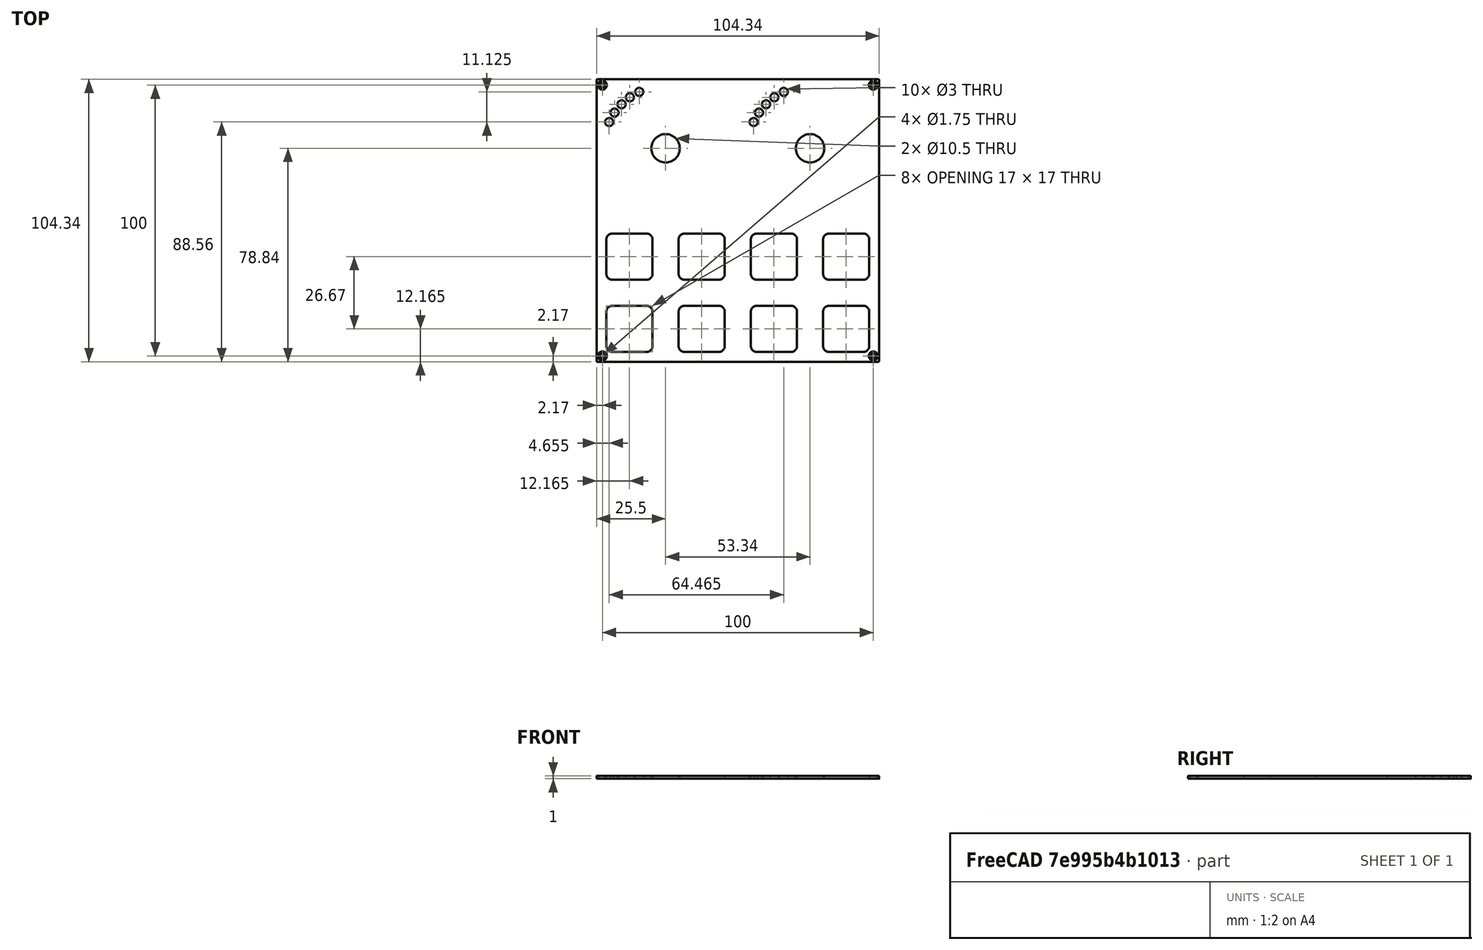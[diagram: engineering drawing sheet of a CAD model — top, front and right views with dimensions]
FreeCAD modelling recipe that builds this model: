
FCSTD DOCUMENT  (FreeCAD 0.21R33771 (Git))
Label: FRONTPANEL-SHEET-VSN0
License: All rights reserved
LicenseURL: https://en.wikipedia.org/wiki/All_rights_reserved
objects: TechDraw::DrawViewDimension×12, TechDraw::DrawViewBalloon×12, TechDraw::DrawHatch×9, Sketcher::SketchObject×7, TechDraw::DrawViewPart×5, TechDraw::DrawViewAnnotation×4, PartDesign::Pocket×3, TechDraw::DrawSVGTemplate×2, PartDesign::Body×2, TechDraw::DrawPage×2, Spreadsheet::Sheet×1, PartDesign::Pad×1, PartDesign::Hole×1, PartDesign::FeatureBase×1, TechDraw::DrawComplexSection×1
note: 40 computed .brp shape members not serialized (recipe doc carries the construction recipe); baked Part::Feature solids carry a one-line shape summary decoded from their .brp

FEATURE [TechDraw::DrawSVGTemplate] Template
  EditableTexts = COLOR=Anodized matte black - RAL code: 9004; CreationDate=2024/08/29; E.G.APPROVED=PRELIMINARY; FC-Scale=1:1; FC-Title=VSN0 - frontpanel; IntechStudioLtd.=Intech Studio Ltd.; MATERIAL=Aluminum 5052-H32; REV=01; STANDARD=ISO 2768 - m
  Height = 297
  Orientation = 1
  Template = <userpath>/Desktop/A3_LandscapeTD_MODIFIED.svg
  Width = 420
FEATURE [Spreadsheet::Sheet] Spreadsheet  label="dim"
  cells = A1='panel_length; B1(panel_length)=104.35; A2='panel_thickness; B2(panel_thickness)=1; A3='panel_radius; B3(panel_radius)==(104.35 - 103.6) / 2; A5='corner_drill_dist; B5(corner_drill_dist)=100; A6='corner_drill_dia; B6(corner_drill_dia)=1.75; A7='corner_drill_countersink; B7(corner_drill_countersink)=3.3; A9='undercut_width; B9(undercut_width)=1; A10='undercut_length; B10(undercut_length)=90; A11='undercut_offset; B11(undercut_offset)=1; A12='undercut_depth; B12(undercut_depth)=0.8; A14='ui_raster; B14(ui_raster)=26.67; A16='light_drill_dia; B16(light_drill_dia)=3; D16='old 2.9; A17='light_bore_dia; B17(light_bore_dia)=3.45; C17='check; D17='old 3.30; E17='DEPRICATED; A18='light_bore_depth; B18(light_bore_depth)=0.4; C18='check; D18='old 0.40; E18='DEPRICATED; A20='pot_drill_dia; B20(pot_drill_dia)=9.8; C20='check; D20='old 6.20; A21='pot_led_dist; B21(pot_led_dist)=8.5; B22=0; A23='but_drill_dia; B23(but_drill_dia)=9.8; A24='but_led_dist; B24(but_led_dist)=8.5; A26='fad_cutout_width; B26(fad_cutout_width)=2.1; C26='check; D26='old 1.50; A27='fad_cutout_length; B27(fad_cutout_length)=36; A28='fad_led_dist; B28(fad_led_dist)=25; A30='enc_drill_dia; B30(enc_drill_dia)=9.8; C30='check; D30='old 6.20; A31='enc_led_dist; B31(enc_led_dist)=8.5; A33='longfad_cutout_width; B33(longfad_cutout_width)=2.1; A34='longfad_cutout_length; B34(longfad_cutout_length)=66; A36='panel_chamfer; B36(panel_chamfer)=0.2; C36='UPDATE DRAWING
FEATURE [Sketcher::SketchObject] Sketch025
  FullyConstrained = true
  MapMode = 5
  Support = -> [XY_Plane011]
  expr: Constraints[49] = <<dim>>.light_drill_dia
  sketch-geometry (28):
    g0: Circle CenterX=-26.67 CenterY=26.67 CenterZ=0 NormalX=0 NormalY=0 NormalZ=1 AngleXU=0 Radius=5.25
    g1: Circle CenterX=26.67 CenterY=26.67 CenterZ=0 NormalX=0 NormalY=0 NormalZ=1 AngleXU=0 Radius=5.25
    g2: LineSegment StartX=-26.67 StartY=26.67 StartZ=0 EndX=0 EndY=26.67 EndZ=0
    g3: LineSegment StartX=0 StartY=26.67 StartZ=0 EndX=0 EndY=0 EndZ=0
    g4: LineSegment StartX=26.67 StartY=26.67 StartZ=0 EndX=0 EndY=26.67 EndZ=0
    g5: Circle CenterX=-26.67 CenterY=26.67 CenterZ=0 NormalX=0 NormalY=0 NormalZ=1 AngleXU=0 Radius=23
    g6: Circle CenterX=26.67 CenterY=26.67 CenterZ=0 NormalX=0 NormalY=0 NormalZ=1 AngleXU=0 Radius=23
    g7: Circle CenterX=-47.5151 CenterY=36.3902 CenterZ=0 NormalX=0 NormalY=0 NormalZ=1 AngleXU=0 Radius=1.5
    g8: Circle CenterX=-45.5105 CenterY=39.8623 CenterZ=0 NormalX=0 NormalY=0 NormalZ=1 AngleXU=0 Radius=1.5
    g9: Circle CenterX=-42.9335 CenterY=42.9335 CenterZ=0 NormalX=0 NormalY=0 NormalZ=1 AngleXU=0 Radius=1.5
    g10: Circle CenterX=-39.8623 CenterY=45.5105 CenterZ=0 NormalX=0 NormalY=0 NormalZ=1 AngleXU=0 Radius=1.5
    g11: Circle CenterX=-36.3902 CenterY=47.5151 CenterZ=0 NormalX=0 NormalY=0 NormalZ=1 AngleXU=0 Radius=1.5
    g12: Circle CenterX=5.82492 CenterY=36.3902 CenterZ=0 NormalX=0 NormalY=0 NormalZ=1 AngleXU=0 Radius=1.5
    g13: Circle CenterX=7.8295 CenterY=39.8623 CenterZ=0 NormalX=0 NormalY=0 NormalZ=1 AngleXU=0 Radius=1.5
    g14: Circle CenterX=10.4065 CenterY=42.9335 CenterZ=0 NormalX=0 NormalY=0 NormalZ=1 AngleXU=0 Radius=1.5
    g15: Circle CenterX=13.4777 CenterY=45.5105 CenterZ=0 NormalX=0 NormalY=0 NormalZ=1 AngleXU=0 Radius=1.5
    g16: Circle CenterX=16.9498 CenterY=47.5151 CenterZ=0 NormalX=0 NormalY=0 NormalZ=1 AngleXU=0 Radius=1.5
    g17: LineSegment StartX=-47.5151 StartY=36.3902 StartZ=0 EndX=5.82492 EndY=36.3902 EndZ=0
    g18: LineSegment StartX=-45.5105 StartY=39.8623 StartZ=0 EndX=7.8295 EndY=39.8623 EndZ=0
    g19: LineSegment StartX=-42.9335 StartY=42.9335 StartZ=0 EndX=10.4065 EndY=42.9335 EndZ=0
    g20: LineSegment StartX=-39.8623 StartY=45.5105 StartZ=0 EndX=13.4777 EndY=45.5105 EndZ=0
    g21: LineSegment StartX=-36.3902 StartY=47.5151 StartZ=0 EndX=16.9498 EndY=47.5151 EndZ=0
    g22: LineSegment StartX=5.82492 StartY=36.3902 StartZ=0 EndX=26.67 EndY=26.67 EndZ=0
    g23: LineSegment StartX=16.9498 StartY=47.5151 StartZ=0 EndX=26.67 EndY=26.67 EndZ=0
    g24: LineSegment StartX=5.82492 StartY=36.3902 StartZ=0 EndX=7.8295 EndY=39.8623 EndZ=0
    g25: LineSegment StartX=7.8295 StartY=39.8623 StartZ=0 EndX=10.4065 EndY=42.9335 EndZ=0
    g26: LineSegment StartX=13.4777 StartY=45.5105 StartZ=0 EndX=10.4065 EndY=42.9335 EndZ=0
    g27: LineSegment StartX=16.9498 StartY=47.5151 StartZ=0 EndX=13.4777 EndY=45.5105 EndZ=0
  constraints (69):
    c: Coincident(g2,g0)
    c: PointOnObject(g2,g-2)
    c: Coincident(g2,g3)
    c: Coincident(g3,g-1)
    c: Coincident(g4,g1)
    c: Coincident(g4,g2)
    c: Equal(g3,g2)
    c: Equal(g2,g4)
    c: Horizontal(g2)
    c: Horizontal(g4)
    c: DistanceY(g3,g3) = 26.67
    c: Equal(g0,g1)
    c: Coincident(g5,g0)
    c: Coincident(g6,g1)
    c: Equal(g6,g5)
    c: PointOnObject(g7,g5)
    c: PointOnObject(g8,g5)
    c: PointOnObject(g9,g5)
    c: PointOnObject(g10,g5)
    c: PointOnObject(g11,g5)
    c: PointOnObject(g12,g6)
    c: PointOnObject(g13,g6)
    c: PointOnObject(g14,g6)
    c: PointOnObject(g15,g6)
    c: PointOnObject(g16,g6)
    c: Equal(g7,g8)
    c: Equal(g8,g9)
    c: Equal(g9,g10)
    c: Equal(g10,g11)
    c: Equal(g11,g12)
    c: Equal(g12,g13)
    c: Equal(g13,g14)
    c: Equal(g14,g15)
    c: Equal(g15,g16)
    c: Coincident(g17,g7)
    c: Coincident(g17,g12)
    c: Coincident(g18,g8)
    c: Coincident(g18,g13)
    c: Horizontal(g18)
    c: Coincident(g19,g9)
    c: Coincident(g19,g14)
    c: Horizontal(g19)
    c: Coincident(g20,g10)
    c: Coincident(g20,g15)
    c: Horizontal(g20)
    c: Coincident(g21,g11)
    c: Horizontal(g21)
    c: Coincident(g21,g16)
    c: Horizontal(g17)
    c: Diameter(g12) = 3
    c: Coincident(g22,g12)
    c: Coincident(g22,g1)
    c: Coincident(g23,g16)
    c: Coincident(g23,g1)
    c: Angle(g22,g4) = 0.436332
    c: Angle(g-2,g23) = 0.436332
    c: Coincident(g24,g12)
    c: Coincident(g24,g13)
    c: Coincident(g25,g13)
    c: Coincident(g26,g15)
    c: Coincident(g26,g25)
    c: Coincident(g27,g16)
    c: Coincident(g27,g15)
    c: Coincident(g25,g14)
    c: Equal(g24,g25)
    c: Equal(g25,g26)
    c: Equal(g26,g27)
    c: Radius(g6) = 23
    c: Diameter(g1) = 10.5
FEATURE [Sketcher::SketchObject] Sketch024
  FullyConstrained = true
  MapMode = 5
  Support = -> [XY_Plane011]
  expr: Constraints[42] = <<dim>>.but_led_dist
  sketch-geometry (17):
    g0: Circle CenterX=-40.005 CenterY=-4.835 CenterZ=0 NormalX=0 NormalY=0 NormalZ=1 AngleXU=0 Radius=2
    g1: Circle CenterX=-13.335 CenterY=-4.835 CenterZ=0 NormalX=0 NormalY=0 NormalZ=1 AngleXU=0 Radius=2
    g2: LineSegment StartX=-40.005 StartY=-4.835 StartZ=0 EndX=-13.335 EndY=-4.835 EndZ=0
    g3: Circle CenterX=13.335 CenterY=-4.835 CenterZ=0 NormalX=0 NormalY=0 NormalZ=1 AngleXU=0 Radius=2
    g4: LineSegment StartX=-13.335 StartY=-4.835 StartZ=0 EndX=13.335 EndY=-4.835 EndZ=0
    g5: Circle CenterX=40.005 CenterY=-4.835 CenterZ=0 NormalX=0 NormalY=0 NormalZ=1 AngleXU=0 Radius=2
    g6: LineSegment StartX=13.335 StartY=-4.835 StartZ=0 EndX=40.005 EndY=-4.835 EndZ=0
    g7: Circle CenterX=-40.005 CenterY=-31.505 CenterZ=0 NormalX=0 NormalY=0 NormalZ=1 AngleXU=0 Radius=2
    g8: LineSegment StartX=-40.005 StartY=-4.835 StartZ=0 EndX=-40.005 EndY=-31.505 EndZ=0
    g9: Circle CenterX=-13.335 CenterY=-31.505 CenterZ=0 NormalX=0 NormalY=0 NormalZ=1 AngleXU=0 Radius=2
    g10: LineSegment StartX=-40.005 StartY=-31.505 StartZ=0 EndX=-13.335 EndY=-31.505 EndZ=0
    g11: Circle CenterX=13.335 CenterY=-31.505 CenterZ=0 NormalX=0 NormalY=0 NormalZ=1 AngleXU=0 Radius=2
    g12: LineSegment StartX=-13.335 StartY=-31.505 StartZ=0 EndX=13.335 EndY=-31.505 EndZ=0
    g13: Circle CenterX=40.005 CenterY=-31.505 CenterZ=0 NormalX=0 NormalY=0 NormalZ=1 AngleXU=0 Radius=2
    g14: LineSegment StartX=13.335 StartY=-31.505 StartZ=0 EndX=40.005 EndY=-31.505 EndZ=0
    g15: LineSegment StartX=-13.335 StartY=-4.835 StartZ=0 EndX=-1.8e-15 EndY=8.5 EndZ=0
    g16: LineSegment StartX=-1.8e-15 StartY=8.5 StartZ=0 EndX=13.335 EndY=-4.835 EndZ=0
  constraints (43):
    c: Diameter(g0) = 4
    c: Coincident(g0,g2)
    c: Coincident(g1,g2)
    c: Coincident(g1,g4)
    c: Coincident(g3,g4)
    c: Coincident(g3,g6)
    c: Coincident(g5,g6)
    c: Coincident(g0,g8)
    c: Coincident(g7,g8)
    c: Coincident(g7,g10)
    c: Coincident(g9,g10)
    c: Coincident(g9,g12)
    c: Coincident(g11,g12)
    c: Coincident(g11,g14)
    c: Coincident(g13,g14)
    c: Horizontal(g4)
    c: Horizontal(g2)
    c: Horizontal(g6)
    c: Horizontal(g10)
    c: Horizontal(g12)
    c: Horizontal(g14)
    c: Vertical(g8)
    c: Equal(g8,g2)
    c: Equal(g2,g10)
    c: Equal(g10,g12)
    c: Equal(g12,g4)
    c: Equal(g4,g6)
    c: Equal(g6,g14)
    c: DistanceX(g4,g4) = 26.67
    c: Equal(g7,g9)
    c: Equal(g9,g11)
    c: Equal(g11,g13)
    c: Equal(g13,g5)
    c: Equal(g5,g3)
    c: Equal(g3,g1)
    c: Equal(g1,g0)
    c: Coincident(g15,g1)
    c: PointOnObject(g15,g-2)
    c: Coincident(g15,g16)
    c: Coincident(g16,g3)
    c: Equal(g16,g15)
    c: Perpendicular(g15,g16)
    c: DistanceY(g-1,g15) = 8.5
FEATURE [Sketcher::SketchObject] Sketch023
  FullyConstrained = true
  MapMode = 5
  Support = -> [XY_Plane011]
  sketch-geometry (97):
    g0: Circle CenterX=-40.005 CenterY=-13.335 CenterZ=0 NormalX=0 NormalY=0 NormalZ=1 AngleXU=0 Radius=2
    g1: Circle CenterX=-13.335 CenterY=-13.335 CenterZ=0 NormalX=0 NormalY=0 NormalZ=1 AngleXU=0 Radius=2
    g2: LineSegment StartX=-40.005 StartY=-13.335 StartZ=0 EndX=-13.335 EndY=-13.335 EndZ=0
    g3: Circle CenterX=13.335 CenterY=-13.335 CenterZ=0 NormalX=0 NormalY=0 NormalZ=1 AngleXU=0 Radius=2
    g4: LineSegment StartX=-13.335 StartY=-13.335 StartZ=0 EndX=13.335 EndY=-13.335 EndZ=0
    g5: Circle CenterX=40.005 CenterY=-13.335 CenterZ=0 NormalX=0 NormalY=0 NormalZ=1 AngleXU=0 Radius=2
    g6: LineSegment StartX=13.335 StartY=-13.335 StartZ=0 EndX=40.005 EndY=-13.335 EndZ=0
    g7: Circle CenterX=-40.005 CenterY=-40.005 CenterZ=0 NormalX=0 NormalY=0 NormalZ=1 AngleXU=0 Radius=2
    g8: LineSegment StartX=-40.005 StartY=-13.335 StartZ=0 EndX=-40.005 EndY=-40.005 EndZ=0
    g9: Circle CenterX=-13.335 CenterY=-40.005 CenterZ=0 NormalX=0 NormalY=0 NormalZ=1 AngleXU=0 Radius=2
    g10: LineSegment StartX=-40.005 StartY=-40.005 StartZ=0 EndX=-13.335 EndY=-40.005 EndZ=0
    g11: Circle CenterX=13.335 CenterY=-40.005 CenterZ=0 NormalX=0 NormalY=0 NormalZ=1 AngleXU=0 Radius=2
    g12: LineSegment StartX=-13.335 StartY=-40.005 StartZ=0 EndX=13.335 EndY=-40.005 EndZ=0
    g13: Circle CenterX=40.005 CenterY=-40.005 CenterZ=0 NormalX=0 NormalY=0 NormalZ=1 AngleXU=0 Radius=2
    g14: LineSegment StartX=13.335 StartY=-40.005 StartZ=0 EndX=40.005 EndY=-40.005 EndZ=0
    g15: LineSegment StartX=0 StartY=0 StartZ=0 EndX=13.335 EndY=-13.335 EndZ=0
    g16: LineSegment StartX=0 StartY=0 StartZ=0 EndX=-13.335 EndY=-13.335 EndZ=0
    g17: LineSegment StartX=-48.505 StartY=-19.735 StartZ=0 EndX=-48.505 EndY=-6.935 EndZ=0
    g18: LineSegment StartX=-46.405 StartY=-4.835 StartZ=0 EndX=-33.605 EndY=-4.835 EndZ=0
    g19: LineSegment StartX=-31.505 StartY=-6.935 StartZ=0 EndX=-31.505 EndY=-19.735 EndZ=0
    g20: LineSegment StartX=-33.605 StartY=-21.835 StartZ=0 EndX=-46.405 EndY=-21.835 EndZ=0
    g21: GeomPoint X=-40.005 Y=-13.335 Z=0
    g22: LineSegment StartX=-21.835 StartY=-19.735 StartZ=0 EndX=-21.835 EndY=-6.935 EndZ=0
    g23: LineSegment StartX=-19.735 StartY=-4.835 StartZ=0 EndX=-6.935 EndY=-4.835 EndZ=0
    g24: LineSegment StartX=-4.835 StartY=-6.935 StartZ=0 EndX=-4.835 EndY=-19.735 EndZ=0
    g25: LineSegment StartX=-6.935 StartY=-21.835 StartZ=0 EndX=-19.735 EndY=-21.835 EndZ=0
    g26: GeomPoint X=-13.335 Y=-13.335 Z=0
    g27: LineSegment StartX=4.835 StartY=-19.735 StartZ=0 EndX=4.835 EndY=-6.935 EndZ=0
    g28: LineSegment StartX=6.935 StartY=-4.835 StartZ=0 EndX=19.735 EndY=-4.835 EndZ=0
    g29: LineSegment StartX=21.835 StartY=-6.935 StartZ=0 EndX=21.835 EndY=-19.735 EndZ=0
    g30: LineSegment StartX=19.735 StartY=-21.835 StartZ=0 EndX=6.935 EndY=-21.835 EndZ=0
    g31: GeomPoint X=13.335 Y=-13.335 Z=0
    g32: LineSegment StartX=31.505 StartY=-19.735 StartZ=0 EndX=31.505 EndY=-6.935 EndZ=0
    g33: LineSegment StartX=33.605 StartY=-4.835 StartZ=0 EndX=46.405 EndY=-4.835 EndZ=0
    g34: LineSegment StartX=48.505 StartY=-6.935 StartZ=0 EndX=48.505 EndY=-19.735 EndZ=0
    g35: LineSegment StartX=46.405 StartY=-21.835 StartZ=0 EndX=33.605 EndY=-21.835 EndZ=0
    g36: GeomPoint X=40.005 Y=-13.335 Z=0
    g37: LineSegment StartX=31.505 StartY=-46.405 StartZ=0 EndX=31.505 EndY=-33.605 EndZ=0
    g38: LineSegment StartX=33.605 StartY=-31.505 StartZ=0 EndX=46.405 EndY=-31.505 EndZ=0
    g39: LineSegment StartX=48.505 StartY=-33.605 StartZ=0 EndX=48.505 EndY=-46.405 EndZ=0
    g40: LineSegment StartX=46.405 StartY=-48.505 StartZ=0 EndX=33.605 EndY=-48.505 EndZ=0
    g41: GeomPoint X=40.005 Y=-40.005 Z=0
    g42: LineSegment StartX=4.835 StartY=-46.405 StartZ=0 EndX=4.835 EndY=-33.605 EndZ=0
    g43: LineSegment StartX=6.935 StartY=-31.505 StartZ=0 EndX=19.735 EndY=-31.505 EndZ=0
    g44: LineSegment StartX=21.835 StartY=-33.605 StartZ=0 EndX=21.835 EndY=-46.405 EndZ=0
    g45: LineSegment StartX=19.735 StartY=-48.505 StartZ=0 EndX=6.935 EndY=-48.505 EndZ=0
    g46: GeomPoint X=13.335 Y=-40.005 Z=0
    g47: LineSegment StartX=-21.835 StartY=-46.405 StartZ=0 EndX=-21.835 EndY=-33.605 EndZ=0
    g48: LineSegment StartX=-19.735 StartY=-31.505 StartZ=0 EndX=-6.935 EndY=-31.505 EndZ=0
    g49: LineSegment StartX=-4.835 StartY=-33.605 StartZ=0 EndX=-4.835 EndY=-46.405 EndZ=0
    g50: LineSegment StartX=-6.935 StartY=-48.505 StartZ=0 EndX=-19.735 EndY=-48.505 EndZ=0
    g51: GeomPoint X=-13.335 Y=-40.005 Z=0
    g52: LineSegment StartX=-48.505 StartY=-46.405 StartZ=0 EndX=-48.505 EndY=-33.605 EndZ=0
    g53: LineSegment StartX=-46.405 StartY=-31.505 StartZ=0 EndX=-33.605 EndY=-31.505 EndZ=0
    g54: LineSegment StartX=-31.505 StartY=-33.605 StartZ=0 EndX=-31.505 EndY=-46.405 EndZ=0
    g55: LineSegment StartX=-33.605 StartY=-48.505 StartZ=0 EndX=-46.405 EndY=-48.505 EndZ=0
    g56: GeomPoint X=-40.005 Y=-40.005 Z=0
    g57: ArcOfCircle CenterX=-46.405 CenterY=-6.935 CenterZ=0 NormalX=0 NormalY=0 NormalZ=1 AngleXU=0 Radius=2.1 StartAngle=1.5708 EndAngle=3.14159
    g58: ArcOfCircle CenterX=-46.405 CenterY=-19.735 CenterZ=0 NormalX=0 NormalY=0 NormalZ=1 AngleXU=0 Radius=2.1 StartAngle=3.14159 EndAngle=4.71239
    g59: ArcOfCircle CenterX=-33.605 CenterY=-19.735 CenterZ=0 NormalX=0 NormalY=0 NormalZ=1 AngleXU=0 Radius=2.1 StartAngle=4.71239 EndAngle=6.28319
    g60: ArcOfCircle CenterX=-33.605 CenterY=-6.935 CenterZ=0 NormalX=0 NormalY=0 NormalZ=1 AngleXU=0 Radius=2.1 StartAngle=0 EndAngle=1.5708
    g61: ArcOfCircle CenterX=-19.735 CenterY=-6.935 CenterZ=0 NormalX=0 NormalY=0 NormalZ=1 AngleXU=0 Radius=2.1 StartAngle=1.5708 EndAngle=3.14159
    g62: ArcOfCircle CenterX=-19.735 CenterY=-19.735 CenterZ=0 NormalX=0 NormalY=0 NormalZ=1 AngleXU=0 Radius=2.1 StartAngle=3.14159 EndAngle=4.71239
    g63: ArcOfCircle CenterX=-6.935 CenterY=-19.735 CenterZ=0 NormalX=0 NormalY=0 NormalZ=1 AngleXU=0 Radius=2.1 StartAngle=4.71239 EndAngle=6.28319
    g64: ArcOfCircle CenterX=-6.935 CenterY=-6.935 CenterZ=0 NormalX=0 NormalY=0 NormalZ=1 AngleXU=0 Radius=2.1 StartAngle=0 EndAngle=1.5708
    g65: ArcOfCircle CenterX=6.935 CenterY=-6.935 CenterZ=0 NormalX=0 NormalY=0 NormalZ=1 AngleXU=0 Radius=2.1 StartAngle=1.5708 EndAngle=3.14159
    g66: ArcOfCircle CenterX=6.935 CenterY=-19.735 CenterZ=0 NormalX=0 NormalY=0 NormalZ=1 AngleXU=0 Radius=2.1 StartAngle=3.14159 EndAngle=4.71239
    g67: ArcOfCircle CenterX=19.735 CenterY=-6.935 CenterZ=0 NormalX=0 NormalY=0 NormalZ=1 AngleXU=0 Radius=2.1 StartAngle=0 EndAngle=1.5708
    g68: ArcOfCircle CenterX=19.735 CenterY=-19.735 CenterZ=0 NormalX=0 NormalY=0 NormalZ=1 AngleXU=0 Radius=2.1 StartAngle=4.71239 EndAngle=6.28319
    g69: ArcOfCircle CenterX=33.605 CenterY=-19.735 CenterZ=0 NormalX=0 NormalY=0 NormalZ=1 AngleXU=0 Radius=2.1 StartAngle=3.14159 EndAngle=4.71239
    g70: ArcOfCircle CenterX=33.605 CenterY=-6.935 CenterZ=0 NormalX=0 NormalY=0 NormalZ=1 AngleXU=0 Radius=2.1 StartAngle=1.5708 EndAngle=3.14159
    g71: ArcOfCircle CenterX=46.405 CenterY=-6.935 CenterZ=0 NormalX=0 NormalY=0 NormalZ=1 AngleXU=0 Radius=2.1 StartAngle=0 EndAngle=1.5708
    g72: ArcOfCircle CenterX=46.405 CenterY=-19.735 CenterZ=0 NormalX=0 NormalY=0 NormalZ=1 AngleXU=0 Radius=2.1 StartAngle=4.71239 EndAngle=6.28319
    g73: ArcOfCircle CenterX=33.605 CenterY=-33.605 CenterZ=0 NormalX=0 NormalY=0 NormalZ=1 AngleXU=0 Radius=2.1 StartAngle=1.5708 EndAngle=3.14159
    g74: ArcOfCircle CenterX=46.405 CenterY=-33.605 CenterZ=0 NormalX=0 NormalY=0 NormalZ=1 AngleXU=0 Radius=2.1 StartAngle=-1.8e-15 EndAngle=1.5708
    g75: ArcOfCircle CenterX=33.605 CenterY=-46.405 CenterZ=0 NormalX=0 NormalY=0 NormalZ=1 AngleXU=0 Radius=2.1 StartAngle=3.14159 EndAngle=4.71239
    g76: ArcOfCircle CenterX=46.405 CenterY=-46.405 CenterZ=0 NormalX=0 NormalY=0 NormalZ=1 AngleXU=0 Radius=2.1 StartAngle=4.71239 EndAngle=6.28319
    g77: ArcOfCircle CenterX=19.735 CenterY=-33.605 CenterZ=0 NormalX=0 NormalY=0 NormalZ=1 AngleXU=0 Radius=2.1 StartAngle=4e-16 EndAngle=1.5708
    g78: ArcOfCircle CenterX=6.935 CenterY=-33.605 CenterZ=0 NormalX=0 NormalY=0 NormalZ=1 AngleXU=0 Radius=2.1 StartAngle=1.5708 EndAngle=3.14159
    g79: ArcOfCircle CenterX=6.935 CenterY=-46.405 CenterZ=0 NormalX=0 NormalY=0 NormalZ=1 AngleXU=0 Radius=2.1 StartAngle=3.14159 EndAngle=4.71239
    g80: ArcOfCircle CenterX=19.735 CenterY=-46.405 CenterZ=0 NormalX=0 NormalY=0 NormalZ=1 AngleXU=0 Radius=2.1 StartAngle=4.71239 EndAngle=6.28319
    g81: ArcOfCircle CenterX=-19.735 CenterY=-33.605 CenterZ=0 NormalX=0 NormalY=0 NormalZ=1 AngleXU=0 Radius=2.1 StartAngle=1.5708 EndAngle=3.14159
    g82: ArcOfCircle CenterX=-6.935 CenterY=-33.605 CenterZ=0 NormalX=0 NormalY=0 NormalZ=1 AngleXU=0 Radius=2.1 StartAngle=1.2e-15 EndAngle=1.5708
    g83: ArcOfCircle CenterX=-6.935 CenterY=-46.405 CenterZ=0 NormalX=0 NormalY=0 NormalZ=1 AngleXU=0 Radius=2.1 StartAngle=4.71239 EndAngle=6.28319
    g84: ArcOfCircle CenterX=-19.735 CenterY=-46.405 CenterZ=0 NormalX=0 NormalY=0 NormalZ=1 AngleXU=0 Radius=2.1 StartAngle=3.14159 EndAngle=4.71239
    g85: ArcOfCircle CenterX=-33.605 CenterY=-33.605 CenterZ=0 NormalX=0 NormalY=0 NormalZ=1 AngleXU=0 Radius=2.1 StartAngle=-1.8e-15 EndAngle=1.5708
    g86: ArcOfCircle CenterX=-33.605 CenterY=-46.405 CenterZ=0 NormalX=0 NormalY=0 NormalZ=1 AngleXU=0 Radius=2.1 StartAngle=4.71239 EndAngle=6.28319
    g87: ArcOfCircle CenterX=-46.405 CenterY=-33.605 CenterZ=0 NormalX=0 NormalY=0 NormalZ=1 AngleXU=0 Radius=2.1 StartAngle=1.5708 EndAngle=3.14159
    g88: ArcOfCircle CenterX=-46.405 CenterY=-46.405 CenterZ=0 NormalX=0 NormalY=0 NormalZ=1 AngleXU=0 Radius=2.1 StartAngle=3.14159 EndAngle=4.71239
    g89: LineSegment StartX=-40.005 StartY=-4.835 StartZ=0 EndX=-40.005 EndY=-21.835 EndZ=0
    g90: LineSegment StartX=-40.005 StartY=-31.505 StartZ=0 EndX=-40.005 EndY=-48.505 EndZ=0
    g91: LineSegment StartX=-13.335 StartY=-31.505 StartZ=0 EndX=-13.335 EndY=-48.505 EndZ=0
    g92: LineSegment StartX=-13.335 StartY=-4.835 StartZ=0 EndX=-13.335 EndY=-21.835 EndZ=0
    g93: LineSegment StartX=13.335 StartY=-4.835 StartZ=0 EndX=13.335 EndY=-21.835 EndZ=0
    g94: LineSegment StartX=13.335 StartY=-31.505 StartZ=0 EndX=13.335 EndY=-48.505 EndZ=0
    g95: LineSegment StartX=40.005 StartY=-4.835 StartZ=0 EndX=40.005 EndY=-21.835 EndZ=0
    g96: LineSegment StartX=40.005 StartY=-31.505 StartZ=0 EndX=40.005 EndY=-48.505 EndZ=0
  constraints (226):
    c: Diameter(g0) = 4
    c: Coincident(g0,g2)
    c: Coincident(g1,g2)
    c: Coincident(g1,g4)
    c: Coincident(g3,g4)
    c: Coincident(g3,g6)
    c: Coincident(g5,g6)
    c: Coincident(g0,g8)
    c: Coincident(g7,g8)
    c: Coincident(g7,g10)
    c: Coincident(g9,g10)
    c: Coincident(g9,g12)
    c: Coincident(g11,g12)
    c: Coincident(g11,g14)
    c: Coincident(g13,g14)
    c: Coincident(g-1,g16)
    c: Coincident(g16,g1)
    c: Coincident(g15,g3)
    c: Horizontal(g4)
    c: Horizontal(g2)
    c: Horizontal(g6)
    c: Horizontal(g10)
    c: Horizontal(g12)
    c: Horizontal(g14)
    c: Vertical(g8)
    c: Equal(g8,g2)
    c: Equal(g2,g10)
    c: Equal(g10,g12)
    c: Equal(g12,g4)
    c: Equal(g4,g6)
    c: Equal(g6,g14)
    c: DistanceX(g4,g4) = 26.67
    c: Equal(g16,g15)
    c: Coincident(g15,g16)
    c: Perpendicular(g15,g16)
    c: Equal(g7,g9)
    c: Equal(g9,g11)
    c: Equal(g11,g13)
    c: Equal(g13,g5)
    c: Equal(g5,g3)
    c: Equal(g3,g1)
    c: Equal(g1,g0)
    c: Horizontal(g18)
    c: Horizontal(g20)
    c: Vertical(g17)
    c: Vertical(g19)
    c: Coincident(g21,g0)
    c: Horizontal(g23)
    c: Horizontal(g25)
    c: Vertical(g22)
    c: Vertical(g24)
    c: Coincident(g26,g1)
    c: Horizontal(g28)
    c: Horizontal(g30)
    c: Vertical(g27)
    c: Vertical(g29)
    c: Coincident(g31,g3)
    c: Horizontal(g33)
    c: Horizontal(g35)
    c: Vertical(g32)
    c: Vertical(g34)
    c: Coincident(g36,g5)
    c: Horizontal(g38)
    c: Horizontal(g40)
    c: Vertical(g37)
    c: Vertical(g39)
    c: Coincident(g41,g13)
    c: Horizontal(g43)
    c: Horizontal(g45)
    c: Vertical(g42)
    c: Vertical(g44)
    c: Coincident(g46,g11)
    c: Horizontal(g48)
    c: Horizontal(g50)
    c: Vertical(g47)
    c: Vertical(g49)
    c: Coincident(g51,g9)
    c: Horizontal(g53)
    c: Horizontal(g55)
    c: Vertical(g52)
    c: Vertical(g54)
    c: Coincident(g56,g7)
    c: Tangent(g18,g57) = 1.5708
    c: Tangent(g17,g57) = 1.5708
    c: Tangent(g17,g58) = 1.5708
    c: Tangent(g20,g58) = 1.5708
    c: Tangent(g19,g59) = 1.5708
    c: Tangent(g20,g59) = 1.5708
    c: Tangent(g19,g60) = 1.5708
    c: Tangent(g18,g60) = 1.5708
    c: Tangent(g23,g61) = 1.5708
    c: Tangent(g22,g61) = 1.5708
    c: Tangent(g25,g62) = 1.5708
    c: Tangent(g22,g62) = 1.5708
    c: Tangent(g24,g63) = 1.5708
    c: Tangent(g25,g63) = 1.5708
    c: Tangent(g24,g64) = 1.5708
    c: Tangent(g23,g64) = 1.5708
    c: Tangent(g28,g65) = 1.5708
    c: Tangent(g27,g65) = 1.5708
    c: Tangent(g27,g66) = 1.5708
    c: Tangent(g30,g66) = 1.5708
    c: Tangent(g29,g67) = 1.5708
    c: Tangent(g28,g67) = 1.5708
    c: Tangent(g29,g68) = 1.5708
    c: Tangent(g30,g68) = 1.5708
    c: Tangent(g32,g69) = 1.5708
    c: Tangent(g35,g69) = 1.5708
    c: Tangent(g33,g70) = 1.5708
    c: Tangent(g32,g70) = 1.5708
    c: Tangent(g33,g71) = 1.5708
    c: Tangent(g34,g71) = 1.5708
    c: Tangent(g34,g72) = 1.5708
    c: Tangent(g35,g72) = 1.5708
    c: Tangent(g38,g73) = 1.5708
    c: Tangent(g37,g73) = 1.5708
    c: Tangent(g38,g74) = 1.5708
    c: Tangent(g39,g74) = 1.5708
    c: Tangent(g37,g75) = 1.5708
    c: Tangent(g40,g75) = 1.5708
    c: Tangent(g39,g76) = 1.5708
    c: Tangent(g40,g76) = 1.5708
    c: Tangent(g44,g77) = 1.5708
    c: Tangent(g43,g77) = 1.5708
    c: Tangent(g43,g78) = 1.5708
    c: Tangent(g42,g78) = 1.5708
    c: Tangent(g42,g79) = 1.5708
    c: Tangent(g45,g79) = 1.5708
    c: Tangent(g44,g80) = 1.5708
    c: Tangent(g45,g80) = 1.5708
    c: Tangent(g48,g81) = 1.5708
    c: Tangent(g47,g81) = 1.5708
    c: Tangent(g48,g82) = 1.5708
    c: Tangent(g49,g82) = 1.5708
    c: Tangent(g49,g83) = 1.5708
    c: Tangent(g50,g83) = 1.5708
    c: Tangent(g47,g84) = 1.5708
    c: Tangent(g50,g84) = 1.5708
    c: Tangent(g53,g85) = 1.5708
    c: Tangent(g54,g85) = 1.5708
    c: Tangent(g54,g86) = 1.5708
    c: Tangent(g55,g86) = 1.5708
    c: Tangent(g53,g87) = 1.5708
    c: Tangent(g52,g87) = 1.5708
    c: Tangent(g52,g88) = 1.5708
    c: Tangent(g55,g88) = 1.5708
    c: Equal(g57,g58)
    c: Equal(g58,g59)
    c: Equal(g59,g60)
    c: Equal(g60,g61)
    c: Equal(g61,g62)
    c: Equal(g62,g63)
    c: Equal(g63,g64)
    c: Equal(g64,g65)
    c: Equal(g65,g66)
    c: Equal(g66,g68)
    c: Equal(g68,g67)
    c: Equal(g67,g70)
    c: Equal(g70,g71)
    c: Equal(g71,g72)
    c: Equal(g72,g69)
    c: Equal(g69,g73)
    c: Equal(g73,g74)
    c: Equal(g74,g76)
    c: Equal(g76,g75)
    c: Equal(g75,g80)
    c: Equal(g80,g77)
    c: Equal(g77,g78)
    c: Equal(g78,g79)
    c: Equal(g79,g83)
    c: Equal(g83,g82)
    c: Equal(g82,g81)
    c: Equal(g81,g84)
    c: Equal(g84,g87)
    c: Equal(g87,g85)
    c: Equal(g85,g86)
    c: Equal(g86,g88)
    c: Equal(g20,g19)
    c: Diameter(g57) = 4.2
    c: Equal(g20,g25)
    c: Equal(g25,g24)
    c: Equal(g24,g30)
    c: Equal(g30,g29)
    c: Equal(g29,g35)
    c: Equal(g35,g34)
    c: Equal(g34,g39)
    c: Equal(g39,g40)
    c: Equal(g40,g44)
    c: Equal(g44,g45)
    c: Equal(g45,g49)
    c: Equal(g49,g50)
    c: Equal(g50,g54)
    c: Equal(g54,g55)
    c: PointOnObject(g89,g20)
    c: Vertical(g89)
    c: PointOnObject(g90,g55)
    c: Vertical(g90)
    c: PointOnObject(g91,g50)
    c: Vertical(g91)
    c: PointOnObject(g92,g25)
    c: PointOnObject(g93,g30)
    c: Vertical(g93)
    c: PointOnObject(g94,g45)
    c: Vertical(g94)
    c: PointOnObject(g95,g35)
    c: Vertical(g95)
    c: PointOnObject(g96,g40)
    c: Vertical(g96)
    c: Symmetric(g18,g18,g89)
    c: Vertical(g92)
    c: Symmetric(g23,g23,g92)
    c: Symmetric(g28,g28,g93)
    c: Symmetric(g33,g33,g95)
    c: Symmetric(g38,g38,g96)
    c: Symmetric(g43,g43,g94)
    c: Symmetric(g48,g48,g91)
    c: Symmetric(g53,g53,g90)
    c: Symmetric(g89,g89,g0)
    c: Symmetric(g92,g92,g1)
    c: Symmetric(g93,g93,g3)
    c: Symmetric(g95,g95,g5)
    c: Symmetric(g96,g96,g13)
    c: Symmetric(g94,g94,g11)
    c: Symmetric(g91,g91,g9)
    c: Symmetric(g90,g90,g7)
    c: DistanceY(g20,g18) = 17
FEATURE [Sketcher::SketchObject] Sketch001
  FullyConstrained = true
  MapMode = 5
  Support = -> [XY_Plane]
  expr: Constraints[13] = <<dim>>.corner_drill_dist
  sketch-geometry (9):
    g0: LineSegment StartX=-50 StartY=50 StartZ=0 EndX=-50 EndY=-50 EndZ=0
    g1: LineSegment StartX=-50 StartY=-50 StartZ=0 EndX=50 EndY=-50 EndZ=0
    g2: LineSegment StartX=50 StartY=-50 StartZ=0 EndX=50 EndY=50 EndZ=0
    g3: LineSegment StartX=50 StartY=50 StartZ=0 EndX=-50 EndY=50 EndZ=0
    g4: Circle CenterX=0 CenterY=0 CenterZ=0 NormalX=0 NormalY=0 NormalZ=1 AngleXU=0 Radius=70.7107
    g5: Circle CenterX=-50 CenterY=50 CenterZ=0 NormalX=0 NormalY=0 NormalZ=1 AngleXU=0 Radius=0.5
    g6: Circle CenterX=50 CenterY=50 CenterZ=0 NormalX=0 NormalY=0 NormalZ=1 AngleXU=0 Radius=0.5
    g7: Circle CenterX=50 CenterY=-50 CenterZ=0 NormalX=0 NormalY=0 NormalZ=1 AngleXU=0 Radius=0.5
    g8: Circle CenterX=-50 CenterY=-50 CenterZ=0 NormalX=0 NormalY=0 NormalZ=1 AngleXU=0 Radius=0.5
  constraints (22):
    c: Coincident(g0,g1)
    c: Coincident(g1,g2)
    c: Coincident(g2,g3)
    c: Coincident(g3,g0)
    c: Equal(g0,g1)
    c: Equal(g0,g2)
    c: Equal(g0,g3)
    c: PointOnObject(g0,g4)
    c: PointOnObject(g1,g4)
    c: PointOnObject(g2,g4)
    c: PointOnObject(g3,g4)
    c: Coincident(g4,g-1)
    c: Horizontal(g3)
    c: DistanceX(g3,g3) = 100
    c: Coincident(g5,g0)
    c: Coincident(g6,g2)
    c: Coincident(g7,g1)
    c: Coincident(g8,g0)
    c: Diameter(g8) = 1
    c: Equal(g8,g7)
    c: Equal(g8,g6)
    c: Equal(g8,g5)
FEATURE [Sketcher::SketchObject] Sketch002
  AttachmentOffset = pos=(0,0,-4.8) rot=(0,0,1;0rad)
  FullyConstrained = true
  MapMode = 5
  Placement = pos=(0,0,-4.8) rot=(0,0,1;0rad)
  Support = -> [XY_Plane]
  expr: .AttachmentOffset.Base.z = -<<dim>>.undercut_depth - 4
  expr: Constraints[91] = <<dim>>.undercut_length
  expr: Constraints[92] = <<dim>>.undercut_width
  expr: Constraints[93] = <<dim>>.panel_length / 2 - <<dim>>.undercut_offset - <<dim>>.undercut_width / 2
  sketch-geometry (40):
    g0: LineSegment StartX=-45 StartY=50.175 StartZ=0 EndX=45 EndY=50.175 EndZ=0
    g1: LineSegment StartX=-45 StartY=51.175 StartZ=0 EndX=45 EndY=51.175 EndZ=0
    g2: LineSegment StartX=-50.675 StartY=45 StartZ=0 EndX=0 EndY=0 EndZ=0
    g3: LineSegment StartX=0 StartY=0 StartZ=0 EndX=-50.675 EndY=-45 EndZ=0
    g4: LineSegment StartX=0 StartY=0 StartZ=0 EndX=-45 EndY=50.675 EndZ=0
    g5: LineSegment StartX=45 StartY=50.675 StartZ=0 EndX=0 EndY=0 EndZ=0
    g6: LineSegment StartX=0 StartY=0 StartZ=0 EndX=50.675 EndY=45 EndZ=0
    g7: LineSegment StartX=50.675 StartY=-45 StartZ=0 EndX=0 EndY=0 EndZ=0
    g8: LineSegment StartX=0 StartY=0 StartZ=0 EndX=45 EndY=-50.675 EndZ=0
    g9: LineSegment StartX=0 StartY=0 StartZ=0 EndX=-45 EndY=-50.675 EndZ=0
    g10: ArcOfCircle CenterX=45 CenterY=50.675 CenterZ=0 NormalX=0 NormalY=0 NormalZ=1 AngleXU=0 Radius=0.5 StartAngle=4.71239 EndAngle=6.28319
    g11: ArcOfCircle CenterX=45 CenterY=50.675 CenterZ=0 NormalX=0 NormalY=0 NormalZ=1 AngleXU=0 Radius=0.5 StartAngle=0 EndAngle=1.5708
    g12: LineSegment StartX=45 StartY=50.675 StartZ=0 EndX=45.5 EndY=50.675 EndZ=0
    g13: ArcOfCircle CenterX=-45 CenterY=50.675 CenterZ=0 NormalX=0 NormalY=0 NormalZ=1 AngleXU=0 Radius=0.5 StartAngle=3.14159 EndAngle=4.71239
    g14: ArcOfCircle CenterX=-45 CenterY=50.675 CenterZ=0 NormalX=0 NormalY=0 NormalZ=1 AngleXU=0 Radius=0.5 StartAngle=1.5708 EndAngle=3.14159
    g15: LineSegment StartX=-45.5 StartY=50.675 StartZ=0 EndX=-45 EndY=50.675 EndZ=0
    g16: LineSegment StartX=-45 StartY=-51.175 StartZ=0 EndX=45 EndY=-51.175 EndZ=0
    g17: LineSegment StartX=-45 StartY=-50.175 StartZ=0 EndX=45 EndY=-50.175 EndZ=0
    g18: ArcOfCircle CenterX=45 CenterY=-50.675 CenterZ=0 NormalX=0 NormalY=0 NormalZ=1 AngleXU=0 Radius=0.5 StartAngle=4.71239 EndAngle=6.28319
    g19: ArcOfCircle CenterX=45 CenterY=-50.675 CenterZ=0 NormalX=0 NormalY=0 NormalZ=1 AngleXU=0 Radius=0.5 StartAngle=0 EndAngle=1.5708
    g20: LineSegment StartX=45 StartY=-50.675 StartZ=0 EndX=45.5 EndY=-50.675 EndZ=0
    g21: ArcOfCircle CenterX=-45 CenterY=-50.675 CenterZ=0 NormalX=0 NormalY=0 NormalZ=1 AngleXU=0 Radius=0.5 StartAngle=3.14159 EndAngle=4.71239
    g22: ArcOfCircle CenterX=-45 CenterY=-50.675 CenterZ=0 NormalX=0 NormalY=0 NormalZ=1 AngleXU=0 Radius=0.5 StartAngle=1.5708 EndAngle=3.14159
    g23: LineSegment StartX=-45.5 StartY=-50.675 StartZ=0 EndX=-45 EndY=-50.675 EndZ=0
    g24: LineSegment StartX=51.175 StartY=-45 StartZ=0 EndX=51.175 EndY=45 EndZ=0
    g25: LineSegment StartX=50.175 StartY=-45 StartZ=0 EndX=50.175 EndY=45 EndZ=0
    g26: ArcOfCircle CenterX=50.675 CenterY=45 CenterZ=0 NormalX=0 NormalY=0 NormalZ=1 AngleXU=0 Radius=0.5 StartAngle=3.8e-15 EndAngle=1.5708
    g27: ArcOfCircle CenterX=50.675 CenterY=45 CenterZ=0 NormalX=0 NormalY=0 NormalZ=1 AngleXU=0 Radius=0.5 StartAngle=1.5708 EndAngle=3.14159
    g28: LineSegment StartX=50.675 StartY=45 StartZ=0 EndX=50.675 EndY=45.5 EndZ=0
    g29: ArcOfCircle CenterX=50.675 CenterY=-45 CenterZ=0 NormalX=0 NormalY=0 NormalZ=1 AngleXU=0 Radius=0.5 StartAngle=4.71239 EndAngle=6.28319
    g30: ArcOfCircle CenterX=50.675 CenterY=-45 CenterZ=0 NormalX=0 NormalY=0 NormalZ=1 AngleXU=0 Radius=0.5 StartAngle=3.14159 EndAngle=4.71239
    g31: LineSegment StartX=50.675 StartY=-45.5 StartZ=0 EndX=50.675 EndY=-45 EndZ=0
    g32: LineSegment StartX=-50.175 StartY=-45 StartZ=0 EndX=-50.175 EndY=45 EndZ=0
    g33: LineSegment StartX=-51.175 StartY=-45 StartZ=0 EndX=-51.175 EndY=45 EndZ=0
    g34: ArcOfCircle CenterX=-50.675 CenterY=45 CenterZ=0 NormalX=0 NormalY=0 NormalZ=1 AngleXU=0 Radius=0.5 StartAngle=1.4e-15 EndAngle=1.5708
    g35: ArcOfCircle CenterX=-50.675 CenterY=45 CenterZ=0 NormalX=0 NormalY=0 NormalZ=1 AngleXU=0 Radius=0.5 StartAngle=1.5708 EndAngle=3.14159
    g36: LineSegment StartX=-50.675 StartY=45 StartZ=0 EndX=-50.675 EndY=45.5 EndZ=0
    g37: ArcOfCircle CenterX=-50.675 CenterY=-45 CenterZ=0 NormalX=0 NormalY=0 NormalZ=1 AngleXU=0 Radius=0.5 StartAngle=4.71239 EndAngle=6.28319
    g38: ArcOfCircle CenterX=-50.675 CenterY=-45 CenterZ=0 NormalX=0 NormalY=0 NormalZ=1 AngleXU=0 Radius=0.5 StartAngle=3.14159 EndAngle=4.71239
    g39: LineSegment StartX=-50.675 StartY=-45.5 StartZ=0 EndX=-50.675 EndY=-45 EndZ=0
  constraints (96):
    c: Horizontal(g0)
    c: Coincident(g2,g-1)
    c: Coincident(g2,g3)
    c: Coincident(g-1,g4)
    c: Coincident(g5,g-1)
    c: Coincident(g5,g6)
    c: Coincident(g7,g-1)
    c: Coincident(g7,g8)
    c: Coincident(g-1,g9)
    c: Equal(g5,g6)
    c: Equal(g6,g8)
    c: Equal(g8,g7)
    c: Equal(g7,g9)
    c: Equal(g9,g3)
    c: Equal(g3,g2)
    c: Equal(g2,g4)
    c: Coincident(g10,g5)
    c: Coincident(g11,g10)
    c: Coincident(g11,g10)
    c: Tangent(g11,g1) = 1.5708
    c: Tangent(g10,g0) = -1.5708
    c: Coincident(g12,g10)
    c: Coincident(g12,g10)
    c: Horizontal(g12)
    c: Coincident(g13,g4)
    c: Coincident(g14,g13)
    c: Coincident(g14,g13)
    c: Tangent(g14,g1) = 1.5708
    c: Tangent(g13,g0) = -1.5708
    c: Coincident(g15,g13)
    c: Coincident(g15,g13)
    c: Horizontal(g15)
    c: Horizontal(g1)
    c: Horizontal(g16)
    c: Coincident(g19,g18)
    c: Coincident(g19,g18)
    c: Tangent(g19,g17) = 1.5708
    c: Tangent(g18,g16) = -1.5708
    c: Coincident(g20,g18)
    c: Coincident(g20,g18)
    c: Horizontal(g20)
    c: Coincident(g22,g21)
    c: Coincident(g22,g21)
    c: Tangent(g22,g17) = 1.5708
    c: Tangent(g21,g16) = -1.5708
    c: Coincident(g23,g21)
    c: Coincident(g23,g21)
    c: Horizontal(g23)
    c: Horizontal(g17)
    c: Coincident(g21,g9)
    c: Coincident(g8,g18)
    c: Equal(g22,g14)
    c: Equal(g17,g1)
    c: Coincident(g27,g26)
    c: Coincident(g27,g26)
    c: Tangent(g27,g25) = 1.5708
    c: Tangent(g26,g24) = -1.5708
    c: Coincident(g28,g26)
    c: Coincident(g28,g26)
    c: Coincident(g30,g29)
    c: Coincident(g30,g29)
    c: Tangent(g30,g25) = 1.5708
    c: Tangent(g29,g24) = -1.5708
    c: Coincident(g31,g29)
    c: Coincident(g31,g29)
    c: Vertical(g31)
    c: Vertical(g28)
    c: Vertical(g25)
    c: Vertical(g24)
    c: Coincident(g35,g34)
    c: Coincident(g35,g34)
    c: Tangent(g35,g33) = 1.5708
    c: Tangent(g34,g32) = -1.5708
    c: Coincident(g36,g34)
    c: Coincident(g36,g34)
    c: Coincident(g38,g37)
    c: Coincident(g38,g37)
    c: Tangent(g38,g33) = 1.5708
    c: Tangent(g37,g32) = -1.5708
    c: Coincident(g39,g37)
    c: Coincident(g39,g37)
    c: Vertical(g39)
    c: Vertical(g36)
    c: Vertical(g33)
    c: Vertical(g32)
    c: Coincident(g6,g26)
    c: Coincident(g7,g29)
    c: Equal(g25,g0)
    c: Equal(g11,g27)
    c: Equal(g1,g33)
    c: Equal(g35,g11)
    c: DistanceX(g13,g10) = 90
    c: Diameter(g13) = 1
    c: DistanceY(g-1,g13) = 50.675
    c: Coincident(g2,g34)
    c: Coincident(g3,g37)
FEATURE [Sketcher::SketchObject] Sketch
  FullyConstrained = true
  MapMode = 5
  Support = -> [XY_Plane]
  expr: Constraints[12] = <<dim>>.panel_radius
  expr: Constraints[16] = <<dim>>.panel_length
  sketch-geometry (11):
    g0: LineSegment StartX=-51.8 StartY=52.175 StartZ=0 EndX=51.8 EndY=52.175 EndZ=0
    g1: LineSegment StartX=52.175 StartY=51.8 StartZ=0 EndX=52.175 EndY=-51.8 EndZ=0
    g2: LineSegment StartX=51.8 StartY=-52.175 StartZ=0 EndX=-51.8 EndY=-52.175 EndZ=0
    g3: LineSegment StartX=-52.175 StartY=-51.8 StartZ=0 EndX=-52.175 EndY=51.8 EndZ=0
    g4: ArcOfCircle CenterX=-51.8 CenterY=51.8 CenterZ=0 NormalX=0 NormalY=0 NormalZ=1 AngleXU=0 Radius=0.375 StartAngle=1.5708 EndAngle=3.14159
    g5: ArcOfCircle CenterX=51.8 CenterY=51.8 CenterZ=0 NormalX=0 NormalY=0 NormalZ=1 AngleXU=0 Radius=0.375 StartAngle=8.4e-15 EndAngle=1.5708
    g6: ArcOfCircle CenterX=51.8 CenterY=-51.8 CenterZ=0 NormalX=0 NormalY=0 NormalZ=1 AngleXU=0 Radius=0.375 StartAngle=4.71239 EndAngle=6.28319
    g7: ArcOfCircle CenterX=-51.8 CenterY=-51.8 CenterZ=0 NormalX=0 NormalY=0 NormalZ=1 AngleXU=0 Radius=0.375 StartAngle=3.14159 EndAngle=4.71239
    g8: LineSegment StartX=-51.8 StartY=51.8 StartZ=0 EndX=0 EndY=0 EndZ=0
    g9: LineSegment StartX=0 StartY=0 StartZ=0 EndX=51.8 EndY=51.8 EndZ=0
    g10: LineSegment StartX=0 StartY=0 StartZ=0 EndX=-51.8 EndY=-51.8 EndZ=0
  constraints (26):
    c: Horizontal(g0)
    c: Horizontal(g2)
    c: Vertical(g1)
    c: Vertical(g3)
    c: Tangent(g3,g4) = 1.5708
    c: Tangent(g0,g4) = 1.5708
    c: Tangent(g0,g5) = 1.5708
    c: Tangent(g1,g5) = 1.5708
    c: Tangent(g1,g6) = 1.5708
    c: Tangent(g2,g6) = 1.5708
    c: Tangent(g2,g7) = 1.5708
    c: Tangent(g3,g7) = 1.5708
    c: Radius(g4) = 0.375
    c: Equal(g4,g5)
    c: Equal(g4,g6)
    c: Equal(g4,g7)
    c: DistanceX(g3,g1) = 104.35
    c: Equal(g3,g0)
    c: Coincident(g8,g4)
    c: Coincident(g8,g-1)
    c: Coincident(g8,g9)
    c: Coincident(g9,g5)
    c: Coincident(g-1,g10)
    c: Coincident(g10,g7)
    c: Equal(g10,g8)
    c: Equal(g8,g9)
FEATURE [PartDesign::Pad] Pad  label="panel"
  AllowMultiFace = false
  Direction = (0,0,1)
  Length = 1
  Length2 = 100
  Profile = -> Sketch
  Reversed = true
  Type = 0
  expr: Length = <<dim>>.panel_thickness
FEATURE [PartDesign::Pocket] Pocket
  AllowMultiFace = false
  BaseFeature = -> Pad
  Direction = (0,0,-1)
  Length = 5
  Length2 = 100
  Profile = -> Sketch002
  Type = 1
FEATURE [PartDesign::Hole] Hole
  BaseFeature = -> Pocket
  CustomThreadClearance = 0
  Depth = 298.105
  DepthType = 1
  Diameter = 1.75
  DrillForDepth = false
  DrillPoint = 1
  DrillPointAngle = 118
  HoleCutCountersinkAngle = 90
  HoleCutCustomValues = false
  HoleCutDepth = 0
  HoleCutDiameter = 3.3
  HoleCutType = 2
  ModelThread = false
  Profile = -> Sketch001
  Tapered = false
  TaperedAngle = 90
  ThreadClass = 0
  ThreadDepth = 298.105
  ThreadDepthType = 0
  ThreadDirection = 0
  ThreadFit = 0
  ThreadSize = 0
  ThreadType = 0
  Threaded = false
  UseCustomThreadClearance = false
  expr: Diameter = <<dim>>.corner_drill_dia
  expr: HoleCutDiameter = <<dim>>.corner_drill_countersink
FEATURE [PartDesign::Body] Body  label="Base"
  Group = -> [Sketch,Pad,Sketch001,Sketch002,Pocket,Hole]
  Origin = -> Origin
  Tip = -> Hole
FEATURE [PartDesign::FeatureBase] Clone009
  BaseFeature = -> Body
FEATURE [PartDesign::Pocket] Pocket007  label="TEK2_TEK_Light"
  BaseFeature = -> Clone009
  Direction = (0,0,-1)
  Length = 5
  Length2 = 5
  Profile = -> Sketch025
  ReferenceAxis = -> Sketch025 [N_Axis]
  Type = 0
FEATURE [Sketcher::SketchObject] Sketch026  label="Section A-A"
  FullyConstrained = true
  MapMode = 5
  Support = -> [XY_Plane011]
  sketch-geometry (1):
    g0: LineSegment StartX=47 StartY=-50 StartZ=0 EndX=54 EndY=-50 EndZ=0
  constraints (4):
    c: Horizontal(g0)
    c: DistanceX(g0,g0) = 7
    c: DistanceY(g0,g-1) = 50
    c: DistanceX(g-1,g0) = 47
FEATURE [TechDraw::DrawViewAnnotation] Annotation
  Font = osifont
  LineSpace = 100
  LockPosition = false
  MaxWidth = -1
  Rotation = 0
  ScaleType = 0
  Text = 10:1
  TextSize = 4
  TextStyle = 0
  X = 279.454
  Y = 86.3155
FEATURE [TechDraw::DrawViewAnnotation] Annotation001
  Font = osifont
  LineSpace = 100
  LockPosition = false
  MaxWidth = -1
  Rotation = 0
  ScaleType = 0
  Text = 1:2
  TextSize = 4
  TextStyle = 0
  X = 181.78
  Y = 49.5973
FEATURE [TechDraw::DrawViewAnnotation] Annotation002
  Font = osifont
  LineSpace = 100
  LockPosition = false
  MaxWidth = -1
  Rotation = 0
  ScaleType = 0
  Text = The mid of the datum plane A is preferred to be near | to the lower limit of the flatness tolerance zone. | It can be achieved with an additional bending step. | Aesthetical surfaces colored red on the view | No scratches, burrs or any kind of damage allowed! | Functional surfaces colored blue on the view (all which perpendicular to the aesthetical) | No burrs or other protruding material allowed!
  TextSize = 3
  TextStyle = 0
  X = 93.479
  Y = 52.5846
FEATURE [TechDraw::DrawSVGTemplate] Template001
  Height = 210
  Orientation = 1
  Template = C:/Program Files/FreeCAD 0.21/data/Mod/TechDraw/Templates/A4_Landscape_blank.svg
  Width = 297
FEATURE [PartDesign::Pocket] Pocket008  label="ButtonPocket"
  BaseFeature = -> Pocket007
  Direction = (0,0,-1)
  Length = 5
  Length2 = 5
  Profile = -> Sketch023
  ReferenceAxis = -> Sketch023 [N_Axis]
  Type = 1
FEATURE [PartDesign::Body] Body011  label="FRONTPANEL-SHEET-VSN0"
  BaseFeature = -> Body
  Group = -> [Clone009,Sketch023,Sketch024,Sketch025,Pocket007,Sketch026,Pocket008]
  Origin = -> Origin011
  Tip = -> Pocket008
FEATURE [TechDraw::DrawViewPart] View
  CoarseView = false
  Direction = (0,0,1)
  Focus = 100
  HardHidden = true
  IsoCount = 0
  IsoHidden = false
  IsoVisible = false
  LockPosition = false
  Perspective = false
  Rotation = 0
  ScaleType = 0
  ScrubCount = 0
  SeamHidden = false
  SeamVisible = true
  SmoothHidden = false
  SmoothVisible = true
  Source = -> [Body011]
  X = 98.8745
  XDirection = (1,0,0)
  Y = 197.053
FEATURE [TechDraw::DrawViewPart] View001
  CoarseView = false
  Direction = (-1,0,0)
  Focus = 100
  HardHidden = true
  IsoCount = 0
  IsoHidden = false
  IsoVisible = false
  LockPosition = false
  Perspective = false
  Rotation = 0
  ScaleType = 0
  ScrubCount = 0
  SeamHidden = false
  SeamVisible = true
  SmoothHidden = false
  SmoothVisible = true
  Source = -> [Body011]
  X = 195.483
  XDirection = (0,0,1)
  Y = 199.908
FEATURE [TechDraw::DrawViewPart] View002
  CoarseView = false
  Direction = (0,0,-1)
  Focus = 100
  HardHidden = true
  IsoCount = 0
  IsoHidden = false
  IsoVisible = false
  LockPosition = false
  Perspective = false
  Rotation = 0
  ScaleType = 0
  ScrubCount = 0
  SeamHidden = false
  SeamVisible = true
  SmoothHidden = false
  SmoothVisible = true
  Source = -> [Body011]
  X = 288.076
  XDirection = (-1,0,0)
  Y = 198.167
FEATURE [TechDraw::DrawViewDimension] Dimension
  AngleOverride = false
  Arbitrary = false
  ArbitraryTolerances = false
  EqualTolerance = false
  ExtensionAngle = 0
  FormatSpec = %.2w
  FormatSpecOverTolerance = %+.2w
  FormatSpecUnderTolerance = %+.2w
  Inverted = false
  LineAngle = 0
  LockPosition = false
  MeasureType = 1
  OverTolerance = 0
  References2D = -> [View]
  Rotation = 0
  ScaleType = 0
  TheoreticalExact = false
  Type = 2
  UnderTolerance = -0.2
  X = 61.7953
  Y = 1.34438
FEATURE [TechDraw::DrawViewDimension] Dimension001
  AngleOverride = false
  Arbitrary = false
  ArbitraryTolerances = false
  EqualTolerance = false
  ExtensionAngle = 0
  FormatSpec = %.2w
  FormatSpecOverTolerance = %+.2w
  FormatSpecUnderTolerance = %+.2w
  Inverted = false
  LineAngle = 0
  LockPosition = false
  MeasureType = 1
  OverTolerance = 0
  References2D = -> [View002]
  Rotation = 0
  ScaleType = 0
  TheoreticalExact = false
  Type = 1
  UnderTolerance = -0.2
  X = -6.41479
  Y = 69.0205
FEATURE [TechDraw::DrawViewBalloon] Balloon
  BubbleShape = 6
  EndType = 6
  EndTypeScale = 1
  KinkLength = -0.1
  LockPosition = false
  OriginX = 70.4982
  OriginY = 52.3109
  Rotation = 0
  ScaleType = 0
  ShapeScale = 1
  SourceView = -> Dimension
  Text = C
  TextWrapLen = -1
  X = 70.6756
  Y = 62.9547
FEATURE [TechDraw::DrawViewBalloon] Balloon001
  BubbleShape = 6
  EndType = 6
  EndTypeScale = 1
  KinkLength = -0.1
  LockPosition = false
  OriginX = -52.3226
  OriginY = 62.1981
  Rotation = 0
  ScaleType = 0
  ShapeScale = 1
  SourceView = -> Dimension001
  Text = B
  TextWrapLen = -1
  X = -60.7084
  Y = 62.1751
FEATURE [TechDraw::DrawViewBalloon] Balloon002
  BubbleShape = 6
  EndType = 0
  EndTypeScale = 1
  KinkLength = -0.1
  LockPosition = false
  OriginX = 0.5
  OriginY = 0
  Rotation = 0
  ScaleType = 0
  ShapeScale = 1
  SourceView = -> View001
  Text = ⏥|0.2
  TextWrapLen = -1
  X = 19.0698
  Y = 0.107397
FEATURE [TechDraw::DrawViewBalloon] Balloon003
  BubbleShape = 6
  EndType = 6
  EndTypeScale = 1
  KinkLength = -0.1
  LockPosition = false
  OriginX = 0.672888
  OriginY = 39.7383
  Rotation = 0
  ScaleType = 0
  ShapeScale = 1
  SourceView = -> View001
  Text = A
  TextWrapLen = -1
  X = 10.7916
  Y = 39.8457
FEATURE [TechDraw::DrawViewBalloon] Balloon008
  BubbleShape = 1
  EndType = 0
  EndTypeScale = 1
  KinkLength = -0.1
  LockPosition = false
  OriginX = -52.0652
  OriginY = 52.0652
  Rotation = 0
  ScaleType = 0
  ShapeScale = 1
  SourceView = -> View
  Text = 4x R0.38
  TextWrapLen = -1
  X = -75.4388
  Y = 68.3556
FEATURE [TechDraw::DrawComplexSection] ComplexSection  label="Section A - A"
  BaseView = -> View
  Caption = Section A-A
  CoarseView = false
  CutSurfaceDisplay = 2
  CuttingToolWireObject = -> Sketch026
  Direction = (1e-16,-1,0)
  FileGeomPattern = C:/Program Files/FreeCAD 0.21/data/Mod/TechDraw/PAT/FCPAT.pat
  FileHatchPattern = C:/Program Files/FreeCAD 0.21/data/Mod/TechDraw/Patterns/simple.svg
  Focus = 100
  FuseBeforeCut = false
  HardHidden = true
  HatchOffset = (0,0,0)
  HatchRotation = 0
  HatchScale = 1
  IsoCount = 0
  IsoHidden = false
  IsoVisible = false
  LockPosition = false
  NameGeomPattern = Gyémánt bevonatú
  Perspective = false
  ProjectionStrategy = 1
  Rotation = 0
  Scale = 10
  ScaleType = 2
  ScrubCount = 0
  SeamHidden = false
  SeamVisible = true
  SectionDirection = 4
  SectionNormal = (1e-16,-1,0)
  SectionOrigin = (0,0,0)
  SectionSymbol = A
  SmoothHidden = false
  SmoothVisible = true
  Source = -> [Body011]
  TrimAfterCut = false
  X = 278.308
  XDirection = (1,1e-16,0)
  Y = 107.09
FEATURE [TechDraw::DrawViewDimension] Dimension010
  AngleOverride = false
  Arbitrary = false
  ArbitraryTolerances = false
  EqualTolerance = true
  ExtensionAngle = 0
  FormatSpec = (%.2w)
  FormatSpecOverTolerance = %+.2w
  FormatSpecUnderTolerance = %+.2w
  Inverted = false
  LineAngle = 0
  LockPosition = false
  MeasureType = 1
  OverTolerance = 0
  References2D = -> [ComplexSection]
  Rotation = 0
  ScaleType = 0
  TheoreticalExact = false
  Type = 2
  UnderTolerance = 0
  X = -36.693
  Y = 2
FEATURE [TechDraw::DrawViewPart] View003
  CoarseView = false
  Direction = (0.57735,0.57735,0.57735)
  Focus = 100
  HardHidden = true
  IsoCount = 0
  IsoHidden = false
  IsoVisible = false
  LockPosition = false
  Perspective = false
  Rotation = 0
  Scale = 0.5
  ScaleType = 2
  ScrubCount = 0
  SeamHidden = false
  SeamVisible = true
  SmoothHidden = false
  SmoothVisible = true
  Source = -> [Body011]
  X = 184.436
  XDirection = (0.707107,0,-0.707107)
  Y = 84.5515
FEATURE [TechDraw::DrawViewBalloon] Balloon013
  BubbleShape = 1
  EndType = 3
  EndTypeScale = 1
  KinkLength = -0.1
  LockPosition = false
  OriginX = -18.2151
  OriginY = -14.1288
  Rotation = 0
  ScaleType = 0
  ShapeScale = 1
  SourceView = -> View003
  TextWrapLen = -1
  X = -113.902
  Y = -52.9975
FEATURE [TechDraw::DrawViewPart] View004
  CoarseView = false
  Direction = (0,0,1)
  Focus = 100
  HardHidden = false
  IsoCount = 0
  IsoHidden = false
  IsoVisible = true
  LockPosition = false
  Perspective = false
  Rotation = 0
  ScaleType = 0
  ScrubCount = 0
  SeamHidden = false
  SeamVisible = true
  SmoothHidden = false
  SmoothVisible = true
  Source = -> [Body011]
  X = 148.5
  XDirection = (1,1e-06,0)
  Y = 105
FEATURE [TechDraw::DrawPage] Page001  label="VSN0_dxf"
  KeepUpdated = true
  NextBalloonIndex = 1
  ProjectionType = 0
  Template = -> Template001
  Views = -> [View004]
FEATURE [TechDraw::DrawHatch] Hatch004  label="Hatch004F56"
  HatchPattern = C:/Program Files/FreeCAD 0.21/data/Mod/TechDraw/Patterns/solid.svg
  Source = -> View003 [Face56,Face3,Face61,Face74,Face75,Face60,Face76]
FEATURE [TechDraw::DrawHatch] Hatch005  label="Hatch005F65"
  HatchPattern = C:/Program Files/FreeCAD 0.21/data/Mod/TechDraw/Patterns/solid.svg
  Source = -> View003 [Face65,Face62,Face72,Face64,Face69,Face59,Face2,Face100]
FEATURE [TechDraw::DrawHatch] Hatch006  label="Hatch006F24"
  HatchPattern = C:/Program Files/FreeCAD 0.21/data/Mod/TechDraw/Patterns/solid.svg
  Source = -> View003 [Face24,Face25,Face57,Face58]
FEATURE [TechDraw::DrawHatch] Hatch007  label="Hatch007F31"
  HatchPattern = C:/Program Files/FreeCAD 0.21/data/Mod/TechDraw/Patterns/solid.svg
  Source = -> View003 [Face31,Face63,Face66,Face30,Face68,Face29,Face32,Face73,Face67,Face27,Face71,Face28,Face70,Face33,Face77,Face26]
FEATURE [TechDraw::DrawViewDimension] Dimension013
  AngleOverride = false
  Arbitrary = false
  ArbitraryTolerances = false
  EqualTolerance = true
  ExtensionAngle = 0
  FormatSpec = 2× ⌀%.2w
  FormatSpecOverTolerance = %+.2w
  FormatSpecUnderTolerance = %+.2w
  Inverted = false
  LineAngle = 0
  LockPosition = false
  MeasureType = 1
  OverTolerance = 0
  References2D = -> [View]
  Rotation = 0
  ScaleType = 0
  TheoreticalExact = false
  Type = 1
  UnderTolerance = 0
  X = -11.3711
  Y = 78.0483
FEATURE [TechDraw::DrawViewBalloon] Balloon020
  BubbleShape = 6
  EndType = 6
  EndTypeScale = 1
  KinkLength = 0
  LockPosition = false
  OriginX = -8.62895
  OriginY = 62.2697
  Rotation = 0
  ScaleType = 0
  ShapeScale = 1
  SourceView = -> View
  Text = ⌖|⌀0.15|A|B|C
  TextWrapLen = -1
  X = 9.30257
  Y = 66.967
FEATURE [TechDraw::DrawViewBalloon] Balloon021
  BubbleShape = 6
  EndType = 6
  EndTypeScale = 1
  KinkLength = 0
  LockPosition = false
  OriginX = -32.134
  OriginY = 72.1105
  Rotation = 0
  ScaleType = 0
  ShapeScale = 1
  SourceView = -> Dimension013
  Text = D
  TextWrapLen = -1
  X = -43.6465
  Y = 72.1571
FEATURE [TechDraw::DrawViewDimension] Dimension014
  AngleOverride = false
  Arbitrary = false
  ArbitraryTolerances = false
  EqualTolerance = true
  ExtensionAngle = 0
  FormatSpec = 8× 4×R%.2w
  FormatSpecOverTolerance = %+.2w
  FormatSpecUnderTolerance = %+.2w
  Inverted = false
  LineAngle = 0
  LockPosition = false
  MeasureType = 1
  OverTolerance = 0
  References2D = -> [View002]
  Rotation = 0
  ScaleType = 0
  TheoreticalExact = false
  Type = 4
  UnderTolerance = 0
  X = 79.3618
  Y = 19.4268
FEATURE [TechDraw::DrawViewDimension] Dimension015
  AngleOverride = false
  Arbitrary = false
  ArbitraryTolerances = false
  EqualTolerance = true
  ExtensionAngle = 0
  FormatSpec = 8× %.2w
  FormatSpecOverTolerance = %+.2w
  FormatSpecUnderTolerance = %+.2w
  Inverted = false
  LineAngle = 0
  LockPosition = false
  MeasureType = 1
  OverTolerance = 0
  References2D = -> [View002]
  Rotation = 0
  ScaleType = 0
  TheoreticalExact = false
  Type = 2
  UnderTolerance = 0
  X = 57.1229
  Y = -38.4799
FEATURE [TechDraw::DrawViewDimension] Dimension016
  AngleOverride = false
  Arbitrary = false
  ArbitraryTolerances = false
  EqualTolerance = true
  ExtensionAngle = 0
  FormatSpec = 8× %.2w
  FormatSpecOverTolerance = %+.2w
  FormatSpecUnderTolerance = %+.2w
  Inverted = false
  LineAngle = 0
  LockPosition = false
  MeasureType = 1
  OverTolerance = 0
  References2D = -> [View002]
  Rotation = 0
  ScaleType = 0
  TheoreticalExact = false
  Type = 1
  UnderTolerance = 0
  X = 39.4138
  Y = -55.8756
FEATURE [TechDraw::DrawViewBalloon] Balloon022
  BubbleShape = 6
  EndType = 0
  EndTypeScale = 1
  KinkLength = 5
  LockPosition = false
  OriginX = 47.7399
  OriginY = -21.0699
  Rotation = 0
  ScaleType = 0
  ShapeScale = 1
  SourceView = -> View002
  Text = ⌓|0.2|A|B|C
  TextWrapLen = -1
  X = 94.7143
  Y = -1.22675
FEATURE [TechDraw::DrawViewAnnotation] Annotation003
  Font = osifont
  LineSpace = 100
  LockPosition = false
  MaxWidth = -1
  Rotation = 0
  ScaleType = 0
  Text = 8x
  TextSize = 4
  TextStyle = 0
  X = 360.241
  Y = 205.9
FEATURE [TechDraw::DrawViewDimension] Dimension017
  AngleOverride = false
  Arbitrary = false
  ArbitraryTolerances = false
  EqualTolerance = true
  ExtensionAngle = 0
  FormatSpec = %.2w
  FormatSpecOverTolerance = %+.2w
  FormatSpecUnderTolerance = %+.2w
  Inverted = false
  LineAngle = 0
  LockPosition = false
  MeasureType = 1
  OverTolerance = 0
  References2D = -> [ComplexSection]
  Rotation = 0
  ScaleType = 0
  TheoreticalExact = false
  Type = 6
  UnderTolerance = 0
  X = -11.8917
  Y = 21.8662
FEATURE [TechDraw::DrawViewDimension] Dimension018
  AngleOverride = false
  Arbitrary = false
  ArbitraryTolerances = false
  EqualTolerance = true
  ExtensionAngle = 0
  FormatSpec = 4× ⌀%.2w
  FormatSpecOverTolerance = %+.2w
  FormatSpecUnderTolerance = %+.2w
  Inverted = false
  LineAngle = 0
  LockPosition = false
  MeasureType = 1
  OverTolerance = 0
  References2D = -> [ComplexSection]
  Rotation = 0
  ScaleType = 0
  TheoreticalExact = false
  Type = 1
  UnderTolerance = 0
  X = 37.2256
  Y = 14.135
FEATURE [TechDraw::DrawViewDimension] Dimension019
  AngleOverride = false
  Arbitrary = false
  ArbitraryTolerances = false
  EqualTolerance = true
  ExtensionAngle = 0
  FormatSpec = 4× ⌀%.2w
  FormatSpecOverTolerance = %+.2w
  FormatSpecUnderTolerance = %+.2w
  Inverted = false
  LineAngle = 0
  LockPosition = false
  MeasureType = 1
  OverTolerance = 0.05
  References2D = -> [ComplexSection]
  Rotation = 0
  ScaleType = 0
  TheoreticalExact = false
  Type = 1
  UnderTolerance = -0.05
  X = 45.6198
  Y = -4.67883
FEATURE [TechDraw::DrawViewBalloon] Balloon023
  BubbleShape = 6
  EndType = 6
  EndTypeScale = 1
  KinkLength = 0
  LockPosition = false
  OriginX = 41.3858
  OriginY = -15.9076
  Rotation = 0
  ScaleType = 0
  ShapeScale = 1
  SourceView = -> Dimension019
  Text = ⌖|⌀0.15|A|B|C
  TextWrapLen = -1
  X = 56.8184
  Y = -15.501
FEATURE [TechDraw::DrawViewDimension] Dimension020
  AngleOverride = false
  Arbitrary = false
  ArbitraryTolerances = false
  EqualTolerance = true
  ExtensionAngle = 0
  FormatSpec = 10× ⌀%.2w
  FormatSpecOverTolerance = %+.2w
  FormatSpecUnderTolerance = %+.2w
  Inverted = false
  LineAngle = 0
  LockPosition = false
  MeasureType = 1
  OverTolerance = 0.05
  References2D = -> [View002]
  Rotation = 0
  ScaleType = 0
  TheoreticalExact = false
  Type = 5
  UnderTolerance = -0.05
  X = 79.8165
  Y = 49.6683
FEATURE [TechDraw::DrawViewBalloon] Balloon024
  BubbleShape = 6
  EndType = 6
  EndTypeScale = 1
  KinkLength = 0
  LockPosition = false
  OriginX = 89.1316
  OriginY = 33.0088
  Rotation = 0
  ScaleType = 0
  ShapeScale = 1
  SourceView = -> Dimension020
  Text = ⌖|⌀0.15|A|B|C
  TextWrapLen = -1
  X = 91.9345
  Y = 38.5855
FEATURE [TechDraw::DrawHatch] Hatch  label="HatchF1"
  HatchPattern = C:/Program Files/FreeCAD 0.21/data/Mod/TechDraw/Patterns/solid.svg
  Source = -> View003 [Face1]
FEATURE [TechDraw::DrawHatch] Hatch008  label="Hatch008F18"
  HatchPattern = C:/Program Files/FreeCAD 0.21/data/Mod/TechDraw/Patterns/solid.svg
  Source = -> View003 [Face18,Face108,Face19,Face38,Face37,Face107,Face41,Face103,Face39,Face93,Face92]
FEATURE [TechDraw::DrawHatch] Hatch009  label="Hatch009F102"
  HatchPattern = C:/Program Files/FreeCAD 0.21/data/Mod/TechDraw/Patterns/solid.svg
  Source = -> View003 [Face102,Face94,Face35,Face97,Face96,Face36,Face104,Face98,Face40,Face105,Face95,Face99,Face101,Face34,Face106]
FEATURE [TechDraw::DrawViewDimension] Dimension021
  AngleOverride = false
  Arbitrary = false
  ArbitraryTolerances = false
  EqualTolerance = true
  ExtensionAngle = 0
  FormatSpec = 2× ⌀%.2w
  FormatSpecOverTolerance = %+.2w
  FormatSpecUnderTolerance = %+.2w
  Inverted = false
  LineAngle = 0
  LockPosition = false
  MeasureType = 1
  OverTolerance = 0
  References2D = -> [View]
  Rotation = 0
  ScaleType = 0
  TheoreticalExact = false
  Type = 5
  UnderTolerance = 0
  X = 61.9519
  Y = 85.6875
FEATURE [TechDraw::DrawViewBalloon] Balloon025
  BubbleShape = 6
  EndType = 6
  EndTypeScale = 1
  KinkLength = 0
  LockPosition = false
  OriginX = 58.933
  OriginY = 73.7204
  Rotation = 0
  ScaleType = 0
  ShapeScale = 1
  SourceView = -> Dimension021
  Text = ◎|⌀0.15|D
  TextWrapLen = -1
  X = 72.1501
  Y = 74.5972
FEATURE [TechDraw::DrawPage] Page  label="VSN0_Drawing"
  KeepUpdated = true
  NextBalloonIndex = 27
  ProjectionType = 0
  Template = -> Template
  Views = -> [View,View001,View002,Dimension,Dimension001,Balloon,Balloon001,Balloon002,Balloon003,Balloon008,ComplexSection,Dimension010,Annotation,View003,Balloon013,Annotation001,Annotation002,Dimension013,Balloon020,Balloon021,Dimension014,Dimension015,Dimension016,Balloon022,Annotation003,Dimension017,Dimension018,Dimension019,Balloon023,Dimension020,Balloon024,Dimension021,Balloon025]
FEATURE [TechDraw::DrawHatch] Hatch010  label="Hatch010F12"
  HatchPattern = C:/Program Files/FreeCAD 0.21/data/Mod/TechDraw/Patterns/solid.svg
  Source = -> View003 [Face12,Face11,Face10,Face17,Face13,Face15,Face14,Face16]
FEATURE [TechDraw::DrawHatch] Hatch011  label="Hatch011F22"
  HatchPattern = C:/Program Files/FreeCAD 0.21/data/Mod/TechDraw/Patterns/solid.svg
  Source = -> View003 [Face22,Face23]
